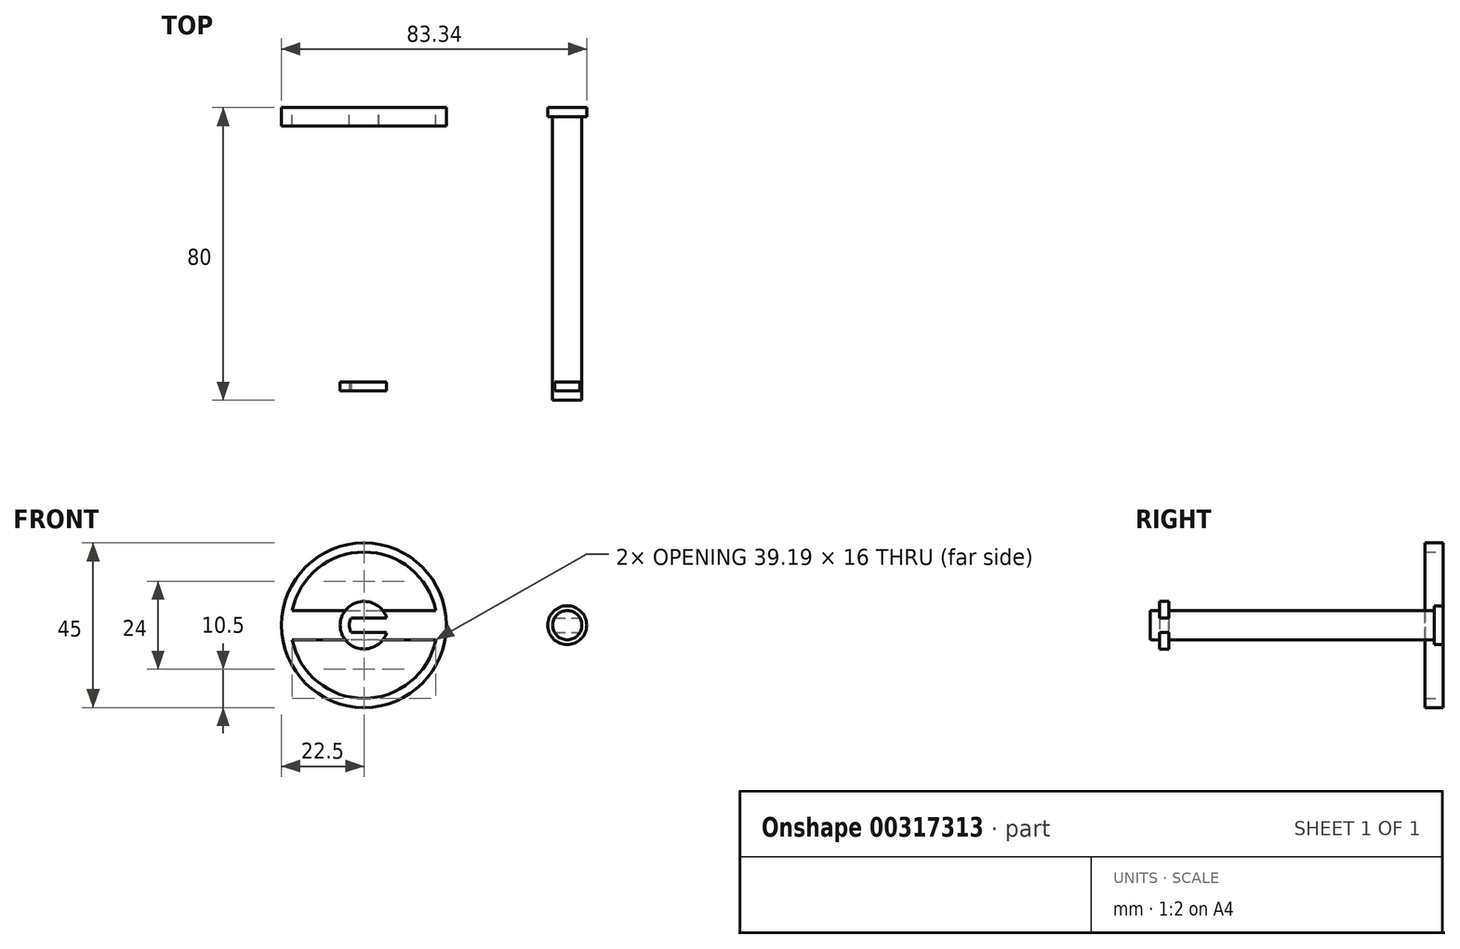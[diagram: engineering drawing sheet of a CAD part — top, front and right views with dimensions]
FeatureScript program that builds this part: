
annotation { "Feature Type Name" : "Feature", "Feature Type Description" : "" }
export const myFeature = defineFeature(function(context is Context, id is Id, definition is map)
    precondition{}
    {
        {
            var Q0;
            Q0=qCreatedBy(makeId("Front.planeOp"),FACE);
            var sketch = newSketch(context, id + "F0", { "sketchPlane" : qUnion([Q0])});
            skCircle(sketch, "E0", {"center": v(0, 0) * mm, "radius": 22.5 * mm});
            skCircle(sketch, "E1", {"center": v(0, 0) * mm, "radius": 20 * mm});
            skLineSegment(sketch, "E2", {"start": v(-20, 0) * mm, "end": v(0, 0) * mm});
            skLineSegment(sketch, "E3", {"start": v(0, 0) * mm, "end": v(20, 0) * mm});
            skLineSegment(sketch, "E4", {"start": v(0, 0) * mm, "end": v(0, 20) * mm});
            skLineSegment(sketch, "E5", {"start": v(0, 0) * mm, "end": v(0, -20) * mm});
            skLineSegment(sketch, "E6", {"start": v(-19.6, 4) * mm, "end": v(0, 4) * mm});
            skLineSegment(sketch, "E7", {"start": v(0, 4) * mm, "end": v(0, -4) * mm});
            skLineSegment(sketch, "E8", {"start": v(0, -4) * mm, "end": v(-20, -4) * mm});
            skLineSegment(sketch, "E9", {"start": v(-4, 0) * mm, "end": v(-4, 19.6) * mm});
            skLineSegment(sketch, "E10", {"start": v(4, 0) * mm, "end": v(4, 19.6) * mm});
            skLineSegment(sketch, "E11", {"start": v(-4, 0) * mm, "end": v(-4, -19.6) * mm});
            skLineSegment(sketch, "E12", {"start": v(4, 0) * mm, "end": v(4, -19.6) * mm});
            skLineSegment(sketch, "E13", {"start": v(0, -4) * mm, "end": v(19.6, -4) * mm});
            skLineSegment(sketch, "E14", {"start": v(0, 4) * mm, "end": v(19.6, 4) * mm});
            skCircle(sketch, "E15", {"center": v(0, 0) * mm, "radius": 4 * mm});
            skCircle(sketch, "E16", {"center": v(0, 0) * mm, "radius": 5.7 * mm});
            skCircle(sketch, "E17", {"center": v(55.53, 0) * mm, "radius": 4 * mm});
            skCircle(sketch, "E18", {"center": v(55.53, 0) * mm, "radius": 5.3 * mm});
            skSolve(sketch);
        }
        {
            var Q0;
            Q0=makeQuery(id+"F0.imprint","IMPRINT",FACE,{"disambiguationData":[TD([[makeQuery(id+"F0.imprint","IMPRINT",EDGE,{"derivedFrom":sQuery(id+"F0.wireOp",EDGE,"E0")}),1.0]])]});
            var Q1;
            {var subQ0=sQuery(id+"F0.wireOp",EDGE,"E2");var subQ1=sQuery(id+"F0.wireOp",EDGE,"E1");var subQ2=makeQuery(id+"F0.imprint","INTERSECT",VERTEX,{"derivedFrom":[subQ1,subQ0]});Q1=makeQuery(id+"F0.imprint","IMPRINT",FACE,{"disambiguationData":[TD([[makeQuery(id+"F0.imprint","IMPRINT",EDGE,{"disambiguationData":[TD([[subQ2,1.0]])],"derivedFrom":subQ1}),1.0]])]});}
            var Q2;
            {var subQ0=sQuery(id+"F0.wireOp",EDGE,"E4");Q2=makeQuery(id+"F0.imprint","IMPRINT",FACE,{"disambiguationData":[TD([[makeQuery(id+"F0.imprint","IMPRINT",EDGE,{"derivedFrom":subQ0}),1.0]])]});}
            var Q3;
            {var subQ0=sQuery(id+"F0.wireOp",EDGE,"E4");Q3=makeQuery(id+"F0.imprint","IMPRINT",FACE,{"disambiguationData":[TD([[makeQuery(id+"F0.imprint","IMPRINT",EDGE,{"derivedFrom":subQ0}),-1.0]])]});}
            var Q4;
            {var subQ0=sQuery(id+"F0.wireOp",EDGE,"E2");var subQ1=sQuery(id+"F0.wireOp",EDGE,"E1");var subQ2=makeQuery(id+"F0.imprint","INTERSECT",VERTEX,{"derivedFrom":[subQ1,subQ0]});Q4=makeQuery(id+"F0.imprint","IMPRINT",FACE,{"disambiguationData":[TD([[makeQuery(id+"F0.imprint","IMPRINT",EDGE,{"disambiguationData":[TD([[subQ2,-1.0]])],"derivedFrom":subQ1}),1.0]])]});}
            var Q5;
            {var subQ1=sQuery(id+"F0.wireOp",EDGE,"E10");var subQ3=sQuery(id+"F0.wireOp",EDGE,"E14");var subQ4=makeQuery(id+"F0.imprint","INTERSECT",VERTEX,{"derivedFrom":[subQ1,subQ3]});Q5=makeQuery(id+"F0.imprint","IMPRINT",FACE,{"disambiguationData":[TD([[makeQuery(id+"F0.imprint","IMPRINT",EDGE,{"disambiguationData":[TD([[subQ4,1.0]])],"derivedFrom":subQ1}),1.0]])]});}
            var Q6;
            {var subQ0=sQuery(id+"F0.wireOp",EDGE,"E3");var subQ1=sQuery(id+"F0.wireOp",EDGE,"E1");var subQ2=makeQuery(id+"F0.imprint","INTERSECT",VERTEX,{"derivedFrom":[subQ1,subQ0]});Q6=makeQuery(id+"F0.imprint","IMPRINT",FACE,{"disambiguationData":[TD([[makeQuery(id+"F0.imprint","IMPRINT",EDGE,{"disambiguationData":[TD([[subQ2,-1.0]])],"derivedFrom":subQ1}),1.0]])]});}
            var Q7;
            {var subQ1=sQuery(id+"F0.wireOp",EDGE,"E6");var subQ3=sQuery(id+"F0.wireOp",EDGE,"E9");var subQ4=makeQuery(id+"F0.imprint","INTERSECT",VERTEX,{"derivedFrom":[subQ1,subQ3]});Q7=makeQuery(id+"F0.imprint","IMPRINT",FACE,{"disambiguationData":[TD([[makeQuery(id+"F0.imprint","IMPRINT",EDGE,{"disambiguationData":[TD([[subQ4,1.0]])],"derivedFrom":subQ3}),-1.0]])]});}
            var Q8;
            {var subQ1=sQuery(id+"F0.wireOp",EDGE,"E8");var subQ3=sQuery(id+"F0.wireOp",EDGE,"E11");var subQ4=makeQuery(id+"F0.imprint","INTERSECT",VERTEX,{"derivedFrom":[subQ1,subQ3]});Q8=makeQuery(id+"F0.imprint","IMPRINT",FACE,{"disambiguationData":[TD([[makeQuery(id+"F0.imprint","IMPRINT",EDGE,{"disambiguationData":[TD([[subQ4,1.0]])],"derivedFrom":subQ3}),1.0]])]});}
            var Q9;
            {var subQ1=sQuery(id+"F0.wireOp",EDGE,"E12");var subQ3=sQuery(id+"F0.wireOp",EDGE,"E13");var subQ4=makeQuery(id+"F0.imprint","INTERSECT",VERTEX,{"derivedFrom":[subQ1,subQ3]});Q9=makeQuery(id+"F0.imprint","IMPRINT",FACE,{"disambiguationData":[TD([[makeQuery(id+"F0.imprint","IMPRINT",EDGE,{"disambiguationData":[TD([[subQ4,1.0]])],"derivedFrom":subQ1}),-1.0]])]});}
            var Q10;
            {var subQ0=sQuery(id+"F0.wireOp",EDGE,"E3");var subQ1=sQuery(id+"F0.wireOp",EDGE,"E1");var subQ2=makeQuery(id+"F0.imprint","INTERSECT",VERTEX,{"derivedFrom":[subQ1,subQ0]});Q10=makeQuery(id+"F0.imprint","IMPRINT",FACE,{"disambiguationData":[TD([[makeQuery(id+"F0.imprint","IMPRINT",EDGE,{"disambiguationData":[TD([[subQ2,1.0]])],"derivedFrom":subQ1}),1.0]])]});}
            var Q11;
            {var subQ0=sQuery(id+"F0.wireOp",EDGE,"E5");Q11=makeQuery(id+"F0.imprint","IMPRINT",FACE,{"disambiguationData":[TD([[makeQuery(id+"F0.imprint","IMPRINT",EDGE,{"derivedFrom":subQ0}),1.0]])]});}
            var Q12;
            {var subQ0=sQuery(id+"F0.wireOp",EDGE,"E5");Q12=makeQuery(id+"F0.imprint","IMPRINT",FACE,{"disambiguationData":[TD([[makeQuery(id+"F0.imprint","IMPRINT",EDGE,{"derivedFrom":subQ0}),-1.0]])]});}
            var Q13;
            {var subQ3=sQuery(id+"F0.wireOp",EDGE,"E16");var subQ5=sQuery(id+"F0.wireOp",EDGE,"E6");var subQ6=makeQuery(id+"F0.imprint","INTERSECT",VERTEX,{"derivedFrom":[subQ5,subQ3]});Q13=makeQuery(id+"F0.imprint","IMPRINT",FACE,{"disambiguationData":[TD([[makeQuery(id+"F0.imprint","IMPRINT",EDGE,{"disambiguationData":[TD([[subQ6,-1.0]])],"derivedFrom":subQ5}),-1.0]])]});}
            var Q14;
            {var subQ0=sQuery(id+"F0.wireOp",EDGE,"E11");var subQ5=sQuery(id+"F0.wireOp",EDGE,"E8");var subQ6=makeQuery(id+"F0.imprint","INTERSECT",VERTEX,{"derivedFrom":[subQ5,subQ0]});Q14=makeQuery(id+"F0.imprint","IMPRINT",FACE,{"disambiguationData":[TD([[makeQuery(id+"F0.imprint","IMPRINT",EDGE,{"disambiguationData":[TD([[subQ6,-1.0]])],"derivedFrom":subQ5}),-1.0]])]});}
            var Q15;
            {var subQ0=sQuery(id+"F0.wireOp",EDGE,"E16");var subQ1=sQuery(id+"F0.wireOp",EDGE,"E6");var subQ2=makeQuery(id+"F0.imprint","INTERSECT",VERTEX,{"derivedFrom":[subQ1,subQ0]});Q15=makeQuery(id+"F0.imprint","IMPRINT",FACE,{"disambiguationData":[TD([[makeQuery(id+"F0.imprint","IMPRINT",EDGE,{"disambiguationData":[TD([[subQ2,-1.0]])],"derivedFrom":subQ1}),1.0]])]});}
            var Q16;
            {var subQ0=sQuery(id+"F0.wireOp",EDGE,"E14");var subQ1=sQuery(id+"F0.wireOp",EDGE,"E10");var subQ2=makeQuery(id+"F0.imprint","INTERSECT",VERTEX,{"derivedFrom":[subQ1,subQ0]});Q16=makeQuery(id+"F0.imprint","IMPRINT",FACE,{"disambiguationData":[TD([[makeQuery(id+"F0.imprint","IMPRINT",EDGE,{"disambiguationData":[TD([[subQ2,-1.0]])],"derivedFrom":subQ1}),-1.0]])]});}
            var Q17;
            {var subQ0=sQuery(id+"F0.wireOp",EDGE,"E13");var subQ1=sQuery(id+"F0.wireOp",EDGE,"E12");var subQ2=makeQuery(id+"F0.imprint","INTERSECT",VERTEX,{"derivedFrom":[subQ1,subQ0]});Q17=makeQuery(id+"F0.imprint","IMPRINT",FACE,{"disambiguationData":[TD([[makeQuery(id+"F0.imprint","IMPRINT",EDGE,{"disambiguationData":[TD([[subQ2,-1.0]])],"derivedFrom":subQ1}),1.0]])]});}
            var Q18;
            {var subQ0=sQuery(id+"F0.wireOp",EDGE,"E12");var subQ5=sQuery(id+"F0.wireOp",EDGE,"E13");var subQ6=makeQuery(id+"F0.imprint","INTERSECT",VERTEX,{"derivedFrom":[subQ0,subQ5]});Q18=makeQuery(id+"F0.imprint","IMPRINT",FACE,{"disambiguationData":[TD([[makeQuery(id+"F0.imprint","IMPRINT",EDGE,{"disambiguationData":[TD([[subQ6,-1.0]])],"derivedFrom":subQ5}),1.0]])]});}
            var Q19;
            {var subQ0=sQuery(id+"F0.wireOp",EDGE,"E10");var subQ5=sQuery(id+"F0.wireOp",EDGE,"E14");var subQ6=makeQuery(id+"F0.imprint","INTERSECT",VERTEX,{"derivedFrom":[subQ0,subQ5]});Q19=makeQuery(id+"F0.imprint","IMPRINT",FACE,{"disambiguationData":[TD([[makeQuery(id+"F0.imprint","IMPRINT",EDGE,{"disambiguationData":[TD([[subQ6,-1.0]])],"derivedFrom":subQ5}),-1.0]])]});}
            var Q20;
            {var subQ0=sQuery(id+"F0.wireOp",EDGE,"E11");var subQ1=sQuery(id+"F0.wireOp",EDGE,"E8");var subQ2=makeQuery(id+"F0.imprint","INTERSECT",VERTEX,{"derivedFrom":[subQ1,subQ0]});Q20=makeQuery(id+"F0.imprint","IMPRINT",FACE,{"disambiguationData":[TD([[makeQuery(id+"F0.imprint","IMPRINT",EDGE,{"disambiguationData":[TD([[subQ2,-1.0]])],"derivedFrom":subQ1}),1.0]])]});}
            extrude(context, id + "F1", {"entities" : qUnion([Q0, Q1, Q2, Q3, Q4, Q5, Q6, Q7, Q8, Q9, Q10, Q11, Q12, Q13, Q14, Q15, Q16, Q17, Q18, Q19, Q20]), "depth" : 5 * mm});
        }
        {
            var Q0;
            Q0=makeQuery(id+"F0.imprint","IMPRINT",FACE,{"disambiguationData":[TD([[makeQuery(id+"F0.imprint","IMPRINT",EDGE,{"derivedFrom":sQuery(id+"F0.wireOp",EDGE,"E17")}),1.0]])]});
            extrude(context, id + "F2", {"entities" : qUnion([Q0]), "depth" : 80 * mm});
        }
        {
            var Q0;
            Q0=makeQuery(id+"F0.imprint","IMPRINT",FACE,{"disambiguationData":[TD([[makeQuery(id+"F0.imprint","IMPRINT",EDGE,{"derivedFrom":sQuery(id+"F0.wireOp",EDGE,"E17")}),-1.0]])]});
            extrude(context, id + "F3", {"entities" : qUnion([Q0]), "operationType" : NewBodyOperationType.ADD, "depth" : 2.5 * mm});
        }
        {
            var Q0;
            Q0=qCreatedBy(makeId("Top.planeOp"),FACE);
            var sketch = newSketch(context, id + "F4", { "sketchPlane" : qUnion([Q0])});
            skPoint(sketch, "E19.0", {"position": v(55.53, 0) * mm});
            skLineSegment(sketch, "E20.0", {"start": v(60.84, -2.5) * mm, "end": v(50.23, -2.5) * mm, "construction": true});
            skPoint(sketch, "E21.endSnap0", {"position": v(55.53, -2.5) * mm});
            skLineSegment(sketch, "E22.0", {"start": v(59.53, -80) * mm, "end": v(51.53, -80) * mm});
            skLineSegment(sketch, "E23", {"start": v(55.53, -2.5) * mm, "end": v(55.53, -75) * mm, "construction": true});
            skLineSegment(sketch, "E24.0", {"start": v(0, 0) * mm, "end": v(20, 0) * mm});
            skLineSegment(sketch, "E25.0", {"start": v(22.5, -5) * mm, "end": v(-22.5, -5) * mm});
            skLineSegment(sketch, "E26", {"start": v(55.53, -75) * mm, "end": v(55.53, -80) * mm});
            skPoint(sketch, "E27", {"position": v(55.53, -77.5) * mm});
            skLineSegment(sketch, "E28", {"start": v(55.53, -75) * mm, "end": v(55.53, -77.5) * mm, "construction": true});
            skPoint(sketch, "E29", {"position": v(55.53, -76.25) * mm});
            skLineSegment(sketch, "E30", {"start": v(51.53, -80) * mm, "end": v(51.53, -2.5) * mm});
            skLineSegment(sketch, "E31", {"start": v(59.53, -2.5) * mm, "end": v(59.53, -80) * mm});
            skLineSegment(sketch, "E32", {"start": v(55.53, -77.5) * mm, "end": v(51.53, -77.5) * mm});
            skLineSegment(sketch, "E33", {"start": v(55.53, -77.5) * mm, "end": v(59.53, -77.5) * mm});
            skLineSegment(sketch, "E34", {"start": v(51.53, -75) * mm, "end": v(59.53, -75) * mm});
            skLineSegment(sketch, "E35", {"start": v(51.53, -75) * mm, "end": v(51.53, -77.5) * mm});
            skLineSegment(sketch, "E36", {"start": v(59.53, -75) * mm, "end": v(59.53, -77.5) * mm});
            skLineSegment(sketch, "E37", {"start": v(51.53, -75) * mm, "end": v(55.53, -75) * mm});
            skLineSegment(sketch, "E38", {"start": v(55.53, -75) * mm, "end": v(59.53, -75) * mm});
            skSolve(sketch);
        }
        {
            var Q0;
            Q0=qCreatedBy(makeId("Top.planeOp"),FACE);
            cPlane(context, id + "F5", {"entities" : qUnion([Q0]), "cplaneType" : CPlaneType.OFFSET, "offset" : 4 * mm, "width" : 150 * mm, "height" : 150 * mm});
        }
        {
            var Q0;
            Q0=qCreatedBy(id+"F5.planeOp",FACE);
            var sketch = newSketch(context, id + "F6", { "sketchPlane" : qUnion([Q0])});
            skLineSegment(sketch, "E39.0", {"start": v(51.53, -75) * mm, "end": v(59.53, -75) * mm});
            skLineSegment(sketch, "E40.0", {"start": v(59.53, -2.5) * mm, "end": v(59.53, -80) * mm});
            skLineSegment(sketch, "E41.0", {"start": v(55.53, -75) * mm, "end": v(55.53, -80) * mm});
            skLineSegment(sketch, "E42", {"start": v(51.53, -80) * mm, "end": v(51.53, -2.5) * mm});
            skPoint(sketch, "E43.0", {"position": v(55.53, -77.5) * mm});
            skPoint(sketch, "E44.0", {"position": v(53.53, -77.5) * mm});
            skPoint(sketch, "E45.0", {"position": v(57.53, -77.5) * mm});
            skLineSegment(sketch, "E46", {"start": v(59.53, -77.5) * mm, "end": v(51.53, -77.5) * mm});
            skSolve(sketch);
        }
        {
            var Q0;
            {var subQ0=sQuery(id+"F6.wireOp",EDGE,"E40.0");var subQ1=sQuery(id+"F6.wireOp",EDGE,"E39.0");var subQ2=makeQuery(id+"F6.imprint","INTERSECT",VERTEX,{"derivedFrom":[subQ1,subQ0]});Q0=makeQuery(id+"F6.imprint","IMPRINT",FACE,{"disambiguationData":[TD([[makeQuery(id+"F6.imprint","IMPRINT",EDGE,{"disambiguationData":[TD([[subQ2,1.0]])],"derivedFrom":subQ1}),-1.0]])]});}
            var Q1;
            {var subQ0=sQuery(id+"F6.wireOp",EDGE,"E42");var subQ1=sQuery(id+"F6.wireOp",EDGE,"E39.0");var subQ2=makeQuery(id+"F6.imprint","INTERSECT",VERTEX,{"derivedFrom":[subQ1,subQ0]});Q1=makeQuery(id+"F6.imprint","IMPRINT",FACE,{"disambiguationData":[TD([[makeQuery(id+"F6.imprint","IMPRINT",EDGE,{"disambiguationData":[TD([[subQ2,-1.0]])],"derivedFrom":subQ1}),-1.0]])]});}
            extrude(context, id + "F7", {"entities" : qUnion([Q0, Q1]), "operationType" : NewBodyOperationType.REMOVE, "oppositeDirection" : true, "depth" : 2 * mm});
        }
        {
            var Q0;
            Q0=qCreatedBy(makeId("Top.planeOp"),FACE);
            cPlane(context, id + "F8", {"entities" : qUnion([Q0]), "cplaneType" : CPlaneType.OFFSET, "offset" : 4 * mm, "oppositeDirection" : true, "width" : 150 * mm, "height" : 150 * mm});
        }
        {
            var Q0;
            Q0=qCreatedBy(id+"F8.planeOp",FACE);
            var sketch = newSketch(context, id + "F9", { "sketchPlane" : qUnion([Q0])});
            skLineSegment(sketch, "E47.0", {"start": v(55.53, -77.5) * mm, "end": v(51.53, -77.5) * mm});
            skLineSegment(sketch, "E48.0", {"start": v(55.53, -75) * mm, "end": v(55.53, -80) * mm});
            skLineSegment(sketch, "E49.0", {"start": v(51.53, -75) * mm, "end": v(59.53, -75) * mm});
            skLineSegment(sketch, "E50", {"start": v(59.53, -2.5) * mm, "end": v(59.53, -80) * mm});
            skLineSegment(sketch, "E51", {"start": v(51.53, -80) * mm, "end": v(51.53, -2.5) * mm});
            skLineSegment(sketch, "E52.0", {"start": v(55.53, -77.5) * mm, "end": v(59.53, -77.5) * mm});
            skSolve(sketch);
        }
        {
            var Q0;
            {var subQ0=sQuery(id+"F9.wireOp",EDGE,"E52.0");Q0=makeQuery(id+"F9.imprint","IMPRINT",FACE,{"disambiguationData":[TD([[makeQuery(id+"F9.imprint","IMPRINT",EDGE,{"derivedFrom":subQ0}),1.0]])]});}
            var Q1;
            {var subQ0=sQuery(id+"F9.wireOp",EDGE,"E47.0");Q1=makeQuery(id+"F9.imprint","IMPRINT",FACE,{"disambiguationData":[TD([[makeQuery(id+"F9.imprint","IMPRINT",EDGE,{"derivedFrom":subQ0}),-1.0]])]});}
            extrude(context, id + "F10", {"entities" : qUnion([Q0, Q1]), "operationType" : NewBodyOperationType.REMOVE, "depth" : 2 * mm});
        }
        {
            var Q0;
            Q0=qCreatedBy(makeId("Right.planeOp"),FACE);
            var sketch = newSketch(context, id + "F11", { "sketchPlane" : qUnion([Q0])});
            skLineSegment(sketch, "E53.0", {"start": v(-77.5, 2) * mm, "end": v(-77.5, 4) * mm});
            skLineSegment(sketch, "E54.0", {"start": v(-75, 2) * mm, "end": v(-75, 4) * mm});
            skLineSegment(sketch, "E55.0", {"start": v(-75, 2) * mm, "end": v(-77.5, 2) * mm});
            skLineSegment(sketch, "E56", {"start": v(-75, 4) * mm, "end": v(-77.5, 4) * mm});
            skLineSegment(sketch, "E57", {"start": v(-75, 2) * mm, "end": v(-75, -6.5) * mm});
            skLineSegment(sketch, "E58", {"start": v(-75, -6.5) * mm, "end": v(-77.5, -6.5) * mm});
            skLineSegment(sketch, "E59", {"start": v(-77.5, -6.5) * mm, "end": v(-77.5, 2) * mm});
            skLineSegment(sketch, "E60", {"start": v(-77.5, 0) * mm, "end": v(-75, 0) * mm});
            skLineSegment(sketch, "E61", {"start": v(-75, 4) * mm, "end": v(-75, 6.5) * mm});
            skLineSegment(sketch, "E62", {"start": v(-75, 6.5) * mm, "end": v(-77.5, 6.5) * mm});
            skLineSegment(sketch, "E63", {"start": v(-77.5, 6.5) * mm, "end": v(-77.5, 4) * mm});
            skLineSegment(sketch, "E64.0", {"start": v(-75, -2) * mm, "end": v(-77.5, -2) * mm});
            skLineSegment(sketch, "E65", {"start": v(-2.5, -4) * mm, "end": v(-80, -4) * mm});
            skSolve(sketch);
        }
        {
            var Q0;
            {var subQ0=sQuery(id+"F11.wireOp",EDGE,"E55.0");Q0=makeQuery(id+"F11.imprint","IMPRINT",FACE,{"disambiguationData":[TD([[makeQuery(id+"F11.imprint","IMPRINT",EDGE,{"derivedFrom":subQ0}),1.0]])]});}
            var Q1;
            Q1=makeQuery(id+"F11.imprint","IMPRINT",FACE,{"disambiguationData":[TD([[makeQuery(id+"F11.imprint","IMPRINT",EDGE,{"derivedFrom":sQuery(id+"F11.wireOp",EDGE,"E53.0")}),-1.0]])]});
            var Q2;
            Q2=makeQuery(id+"F11.imprint","IMPRINT",FACE,{"disambiguationData":[TD([[makeQuery(id+"F11.imprint","IMPRINT",EDGE,{"derivedFrom":sQuery(id+"F11.wireOp",EDGE,"E56")}),-1.0]])]});
            var Q3;
            Q3=sQuery(id+"F11.wireOp",EDGE,"E60");
            revolve(context, id + "F12", {"entities" : qUnion([Q0, Q1, Q2]), "axis" : qUnion([Q3]), "revolveType" : RevolveType.FULL});
        }
        {
            var Q0;
            Q0=makeQuery(id+"F12.opRevolve","SWEPT_FACE",FACE,{"disambiguationData":[OSD([sQuery(id+"F11.wireOp",EDGE,"E53.0"),sQuery(id+"F11.wireOp",EDGE,"E59"),sQuery(id+"F11.wireOp",EDGE,"E63")])]});
            var sketch = newSketch(context, id + "F13", { "sketchPlane" : qUnion([Q0])});
            skCircle(sketch, "E66", {"center": v(0, 0) * mm, "radius": 4 * mm});
            skPoint(sketch, "E67.0", {"position": v(0, 2) * mm});
            skPoint(sketch, "E68.0", {"position": v(0, 4) * mm});
            skLineSegment(sketch, "E69", {"start": v(0, -4) * mm, "end": v(0, -6.5) * mm});
            skLineSegment(sketch, "E70.0", {"start": v(0, 4) * mm, "end": v(0, -4) * mm});
            skLineSegment(sketch, "E71.0", {"start": v(22.5, 0) * mm, "end": v(-22.5, 0) * mm});
            skLineSegment(sketch, "E72", {"start": v(0, 2) * mm, "end": v(6.18, 2) * mm});
            skLineSegment(sketch, "E73", {"start": v(0, 2) * mm, "end": v(-3.46, 2) * mm});
            skPoint(sketch, "E74.0", {"position": v(0, -2) * mm});
            skLineSegment(sketch, "E75", {"start": v(0, -2) * mm, "end": v(6.18, -2) * mm});
            skLineSegment(sketch, "E76", {"start": v(0, -2) * mm, "end": v(-3.46, -2) * mm});
            skSolve(sketch);
        }
        {
            var Q0;
            {var subQ0=sQuery(id+"F13.wireOp",EDGE,"E72");var subQ1=sQuery(id+"F13.wireOp",EDGE,"E66");var subQ2=makeQuery(id+"F13.imprint","INTERSECT",VERTEX,{"derivedFrom":[subQ1,subQ0]});Q0=makeQuery(id+"F13.imprint","IMPRINT",FACE,{"disambiguationData":[TD([[makeQuery(id+"F13.imprint","IMPRINT",EDGE,{"disambiguationData":[TD([[subQ2,1.0]])],"derivedFrom":subQ1}),1.0]])]});}
            var Q1;
            {var subQ0=sQuery(id+"F13.wireOp",EDGE,"E72");var subQ1=sQuery(id+"F13.wireOp",EDGE,"E66");var subQ2=makeQuery(id+"F13.imprint","INTERSECT",VERTEX,{"derivedFrom":[subQ1,subQ0]});Q1=makeQuery(id+"F13.imprint","IMPRINT",FACE,{"disambiguationData":[TD([[makeQuery(id+"F13.imprint","IMPRINT",EDGE,{"disambiguationData":[TD([[subQ2,1.0]])],"derivedFrom":subQ1}),-1.0]])]});}
            var Q2;
            {var subQ1=sQuery(id+"F13.wireOp",EDGE,"E66");var subQ3=sQuery(id+"F13.wireOp",EDGE,"E71.0");var subQ4=makeQuery(id+"F13.imprint","INTERSECT",VERTEX,{"disambiguationData":[OD(0.0)],"derivedFrom":[subQ1,subQ3]});Q2=makeQuery(id+"F13.imprint","IMPRINT",FACE,{"disambiguationData":[TD([[makeQuery(id+"F13.imprint","IMPRINT",EDGE,{"disambiguationData":[TD([[subQ4,-1.0]])],"derivedFrom":subQ3}),1.0]])]});}
            var Q3;
            {var subQ1=sQuery(id+"F13.wireOp",EDGE,"E66");var subQ3=sQuery(id+"F13.wireOp",EDGE,"E71.0");var subQ4=makeQuery(id+"F13.imprint","INTERSECT",VERTEX,{"disambiguationData":[OD(1.0)],"derivedFrom":[subQ1,subQ3]});Q3=makeQuery(id+"F13.imprint","IMPRINT",FACE,{"disambiguationData":[TD([[makeQuery(id+"F13.imprint","IMPRINT",EDGE,{"disambiguationData":[TD([[subQ4,1.0]])],"derivedFrom":subQ3}),1.0]])]});}
            var Q4;
            {var subQ0=sQuery(id+"F13.wireOp",EDGE,"E73");Q4=makeQuery(id+"F13.imprint","IMPRINT",FACE,{"disambiguationData":[TD([[makeQuery(id+"F13.imprint","IMPRINT",EDGE,{"derivedFrom":subQ0}),1.0]])]});}
            var Q5;
            {var subQ0=sQuery(id+"F13.wireOp",EDGE,"E71.0");var subQ1=sQuery(id+"F13.wireOp",EDGE,"E66");var subQ2=makeQuery(id+"F13.imprint","INTERSECT",VERTEX,{"disambiguationData":[OD(0.0)],"derivedFrom":[subQ1,subQ0]});Q5=makeQuery(id+"F13.imprint","IMPRINT",FACE,{"disambiguationData":[TD([[makeQuery(id+"F13.imprint","IMPRINT",EDGE,{"disambiguationData":[TD([[subQ2,1.0]])],"derivedFrom":subQ1}),-1.0]])]});}
            extrude(context, id + "F14", {"entities" : qUnion([Q0, Q1, Q2, Q3, Q4, Q5]), "operationType" : NewBodyOperationType.REMOVE, "oppositeDirection" : true, "depth" : 25 * mm});
        }
    });
